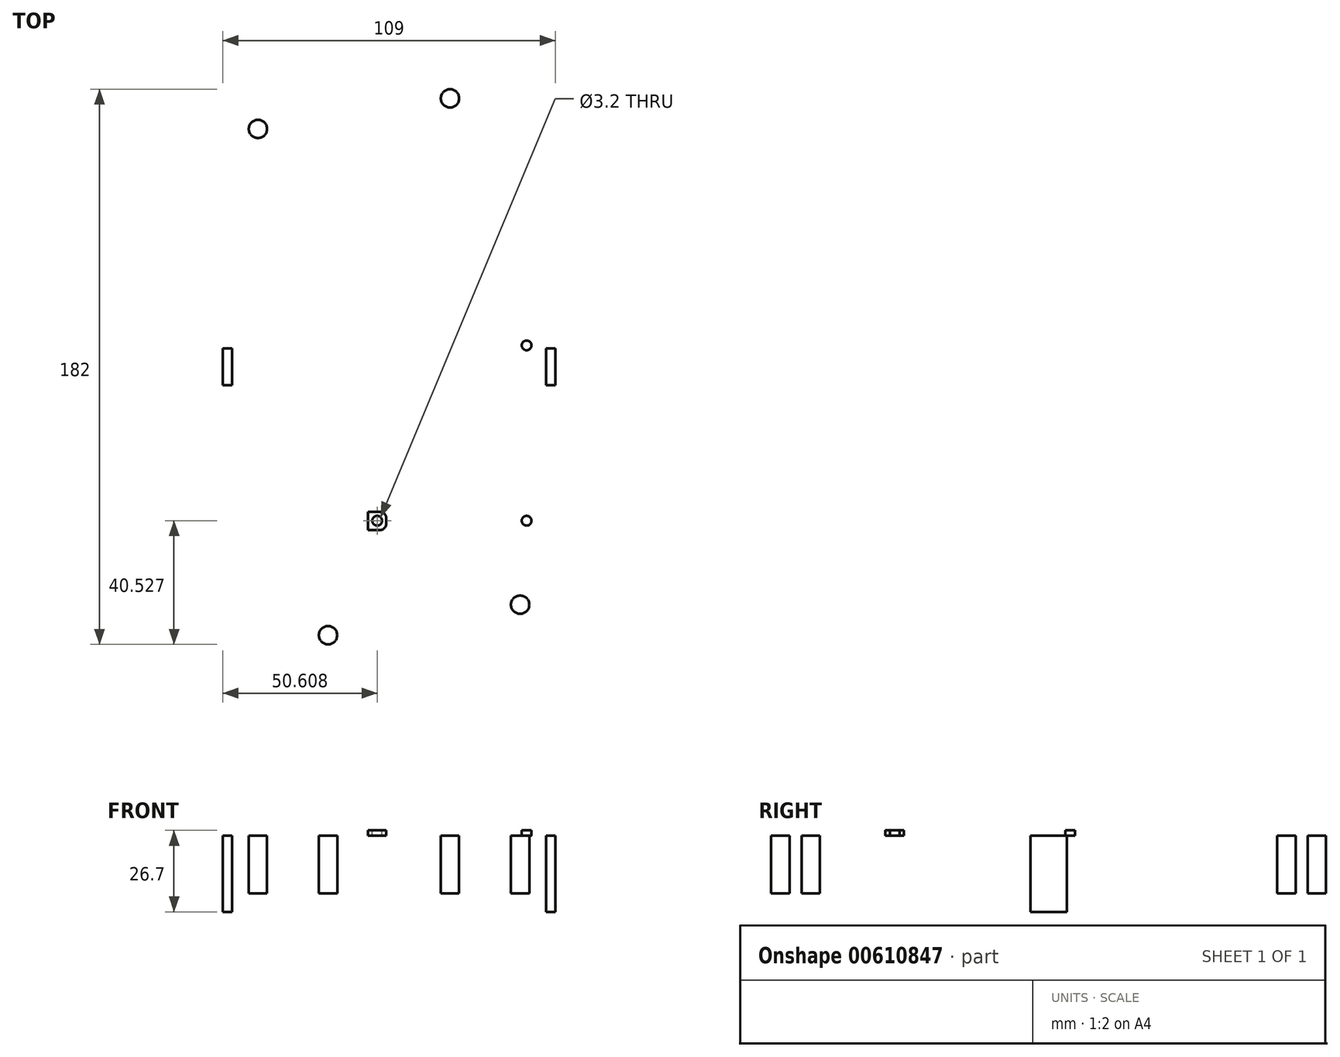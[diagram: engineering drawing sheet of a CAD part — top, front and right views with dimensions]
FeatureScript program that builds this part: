
annotation { "Feature Type Name" : "Feature", "Feature Type Description" : "" }
export const myFeature = defineFeature(function(context is Context, id is Id, definition is map)
    precondition{}
    {
        {
            var Q0;
            Q0=qCreatedBy(makeId("Top.planeOp"),FACE);
            var sketch = newSketch(context, id + "F0", { "sketchPlane" : qUnion([Q0])});
            skLineSegment(sketch, "E0.bottom", {"start": v(56, 96) * mm, "end": v(-56, 96) * mm});
            skLineSegment(sketch, "E0.top", {"start": v(56, -96) * mm, "end": v(-56, -96) * mm});
            skLineSegment(sketch, "E0.left", {"start": v(56, 96) * mm, "end": v(56, -96) * mm});
            skLineSegment(sketch, "E0.right", {"start": v(-56, 96) * mm, "end": v(-56, -96) * mm});
            skPoint(sketch, "E0.middle", {"position": v(0, 0) * mm});
            skLineSegment(sketch, "E1.MirrorCS", {"start": v(-41, 85) * mm, "end": v(-56, 85) * mm});
            skCircle(sketch, "E2.MirrorC", {"center": v(-43, 78) * mm, "radius": 1.6 * mm});
            skLineSegment(sketch, "E3", {"start": v(0, 96) * mm, "end": v(0, -96) * mm, "construction": true});
            skLineSegment(sketch, "E4", {"start": v(-36, 90) * mm, "end": v(-36, 96) * mm});
            skPoint(sketch, "E5.visualSharp", {"position": v(-36, 85) * mm});
            skArc(sketch, "E5.filletArc", {"start": v(-41, 85) * mm, "mid": v(-37.46, 86.46) * mm, "end": v(-36, 90) * mm});
            skArc(sketch, "E6.MirrorCS", {"start": v(41, 85) * mm, "mid": v(37.46, 86.46) * mm, "end": v(36, 90) * mm});
            skLineSegment(sketch, "E7.MirrorCS", {"start": v(41, 85) * mm, "end": v(56, 85) * mm});
            skLineSegment(sketch, "E8.MirrorCS", {"start": v(36, 90) * mm, "end": v(36, 96) * mm});
            skPoint(sketch, "E9.MirrorP", {"position": v(36, 85) * mm});
            skCircle(sketch, "E10.MirrorC", {"center": v(43, 78) * mm, "radius": 1.6 * mm});
            skLineSegment(sketch, "E11", {"start": v(-56, 0) * mm, "end": v(56, 0) * mm, "construction": true});
            skArc(sketch, "E12.MirrorCS", {"start": v(-41, -85) * mm, "mid": v(-37.46, -86.46) * mm, "end": v(-36, -90) * mm});
            skLineSegment(sketch, "E13.MirrorCS", {"start": v(-36, -90) * mm, "end": v(-36, -96) * mm});
            skLineSegment(sketch, "E14.MirrorCS", {"start": v(36, -90) * mm, "end": v(36, -96) * mm});
            skArc(sketch, "E15.MirrorCS", {"start": v(41, -85) * mm, "mid": v(37.46, -86.46) * mm, "end": v(36, -90) * mm});
            skCircle(sketch, "E16.MirrorC", {"center": v(-43, -78) * mm, "radius": 1.6 * mm});
            skLineSegment(sketch, "E17.MirrorCS", {"start": v(-41, -85) * mm, "end": v(-56, -85) * mm});
            skCircle(sketch, "E18.MirrorC", {"center": v(43, -78) * mm, "radius": 1.6 * mm});
            skPoint(sketch, "E19.MirrorP", {"position": v(36, -85) * mm});
            skLineSegment(sketch, "E20.MirrorCS", {"start": v(41, -85) * mm, "end": v(56, -85) * mm});
            skPoint(sketch, "E21.MirrorP", {"position": v(-36, -85) * mm});
            skCircle(sketch, "E22", {"center": v(-46, 7.1) * mm, "radius": 3 * mm});
            skCircle(sketch, "E23.1.0.0", {"center": v(-34, 7.1) * mm, "radius": 3 * mm});
            skCircle(sketch, "E23.2.0.0", {"center": v(-22, 7.1) * mm, "radius": 3 * mm});
            skLineSegment(sketch, "E23.direction1", {"start": v(-46, 7.1) * mm, "end": v(-34, 7.1) * mm, "construction": true});
            skCircle(sketch, "E24", {"center": v(-49, 0) * mm, "radius": 2 * mm});
            skCircle(sketch, "E25.1.0.0", {"center": v(-43, 0) * mm, "radius": 2 * mm});
            skLineSegment(sketch, "E25.direction1", {"start": v(-49, 0) * mm, "end": v(-43, 0) * mm, "construction": true});
            skCircle(sketch, "E26.1.0.0", {"center": v(-37, 0) * mm, "radius": 2 * mm});
            skCircle(sketch, "E26.1.0.1", {"center": v(-31, 0) * mm, "radius": 2 * mm});
            skCircle(sketch, "E26.2.0.0", {"center": v(-25, 0) * mm, "radius": 2 * mm});
            skCircle(sketch, "E26.2.0.1", {"center": v(-19, 0) * mm, "radius": 2 * mm});
            skLineSegment(sketch, "E26.direction1", {"start": v(-49, 0) * mm, "end": v(-37, 0) * mm, "construction": true});
            skSolve(sketch);
        }
        {
            var Q0;
            Q0=makeQuery(id+"F0.imprint","IMPRINT",FACE,{"disambiguationData":[TD([[makeQuery(id+"F0.imprint","IMPRINT",EDGE,{"derivedFrom":sQuery(id+"F0.wireOp",EDGE,"E0.bottom")}),1.0]])]});
            var sketch = newSketch(context, id + "F1", { "sketchPlane" : qUnion([Q0])});
            skLineSegment(sketch, "E27.bottom", {"start": v(-40.64, 23.04) * mm, "end": v(-40.64, 44.87) * mm});
            skLineSegment(sketch, "E27.left", {"start": v(-40.64, 23.04) * mm, "end": v(-19.64, 23.04) * mm});
            skLineSegment(sketch, "E27.right", {"start": v(-40.64, 73.84) * mm, "end": v(-19.64, 73.84) * mm});
            skPoint(sketch, "E27.middle", {"position": v(0, 48.44) * mm});
            skCircle(sketch, "E28", {"center": v(-37.14, 48.37) * mm, "radius": 1.59 * mm});
            skLineSegment(sketch, "E29.top", {"start": v(-33.64, 49.87) * mm, "end": v(-33.64, 46.87) * mm});
            skLineSegment(sketch, "E29.left", {"start": v(-40.64, 51.87) * mm, "end": v(-35.64, 51.87) * mm});
            skLineSegment(sketch, "E29.right", {"start": v(-40.64, 44.87) * mm, "end": v(-35.64, 44.87) * mm});
            skLineSegment(sketch, "E30", {"start": v(0, 23.04) * mm, "end": v(0, 25.04) * mm, "construction": true});
            skLineSegment(sketch, "E31.trimOffspring", {"start": v(-40.64, 51.87) * mm, "end": v(-40.64, 73.84) * mm});
            skLineSegment(sketch, "E32.MirrorCS", {"start": v(40.64, 23.04) * mm, "end": v(40.64, 44.87) * mm});
            skLineSegment(sketch, "E33.MirrorCS", {"start": v(40.64, 44.87) * mm, "end": v(35.64, 44.87) * mm});
            skLineSegment(sketch, "E34.MirrorCS", {"start": v(33.64, 49.87) * mm, "end": v(33.64, 46.87) * mm});
            skLineSegment(sketch, "E35.MirrorCS", {"start": v(40.64, 51.87) * mm, "end": v(35.64, 51.87) * mm});
            skLineSegment(sketch, "E36.MirrorCS", {"start": v(40.64, 51.87) * mm, "end": v(40.64, 73.84) * mm});
            skLineSegment(sketch, "E37.bottom", {"start": v(-19.64, 18.04) * mm, "end": v(-19.64, 18.04) * mm});
            skLineSegment(sketch, "E37.top", {"start": v(19.64, 18.04) * mm, "end": v(19.64, 18.04) * mm});
            skLineSegment(sketch, "E37.left", {"start": v(-17.64, 25.04) * mm, "end": v(17.64, 25.04) * mm});
            skLineSegment(sketch, "E38.trimOffspring", {"start": v(19.64, 23.04) * mm, "end": v(40.64, 23.04) * mm});
            skLineSegment(sketch, "E39.MirrorCS", {"start": v(-19.64, 68.84) * mm, "end": v(-19.64, 68.84) * mm});
            skLineSegment(sketch, "E40.MirrorCS", {"start": v(-17.64, 71.84) * mm, "end": v(17.64, 71.84) * mm});
            skLineSegment(sketch, "E41.MirrorCS", {"start": v(19.64, 68.84) * mm, "end": v(19.64, 68.84) * mm});
            skLineSegment(sketch, "E42.trimOffspring", {"start": v(19.64, 73.84) * mm, "end": v(40.64, 73.84) * mm});
            skPoint(sketch, "E43.visualSharp", {"position": v(-33.64, 51.87) * mm});
            skArc(sketch, "E43.filletArc", {"start": v(-33.64, 49.87) * mm, "mid": v(-34.22, 51.29) * mm, "end": v(-35.64, 51.87) * mm});
            skPoint(sketch, "E44.visualSharp", {"position": v(-33.64, 44.87) * mm});
            skArc(sketch, "E44.filletArc", {"start": v(-35.64, 44.87) * mm, "mid": v(-34.22, 45.46) * mm, "end": v(-33.64, 46.87) * mm});
            skPoint(sketch, "E45.visualSharp", {"position": v(33.64, 51.87) * mm});
            skArc(sketch, "E45.filletArc", {"start": v(35.64, 51.87) * mm, "mid": v(34.23, 51.29) * mm, "end": v(33.64, 49.87) * mm});
            skPoint(sketch, "E46.visualSharp", {"position": v(33.64, 44.87) * mm});
            skArc(sketch, "E46.filletArc", {"start": v(33.64, 46.87) * mm, "mid": v(34.23, 45.46) * mm, "end": v(35.64, 44.87) * mm});
            skPoint(sketch, "E47.visualSharp", {"position": v(-19.64, 25.04) * mm});
            skArc(sketch, "E47.filletArc", {"start": v(-17.64, 25.04) * mm, "mid": v(-19.05, 24.45) * mm, "end": v(-19.64, 23.04) * mm});
            skPoint(sketch, "E48.visualSharp", {"position": v(19.64, 25.04) * mm});
            skArc(sketch, "E48.filletArc", {"start": v(19.64, 23.04) * mm, "mid": v(19.06, 24.45) * mm, "end": v(17.64, 25.04) * mm});
            skPoint(sketch, "E49.visualSharp", {"position": v(-19.64, 71.84) * mm});
            skArc(sketch, "E49.filletArc", {"start": v(-19.64, 73.84) * mm, "mid": v(-19.05, 72.42) * mm, "end": v(-17.64, 71.84) * mm});
            skPoint(sketch, "E50.visualSharp", {"position": v(19.64, 71.84) * mm});
            skArc(sketch, "E50.filletArc", {"start": v(17.64, 71.84) * mm, "mid": v(19.06, 72.42) * mm, "end": v(19.64, 73.84) * mm});
            skCircle(sketch, "E51.MirrorC", {"center": v(37.14, 48.37) * mm, "radius": 1.59 * mm});
            skSolve(sketch);
        }
        {
            var Q0;
            Q0=makeQuery(id+"F0.imprint","IMPRINT",FACE,{"disambiguationData":[TD([[makeQuery(id+"F0.imprint","IMPRINT",EDGE,{"derivedFrom":sQuery(id+"F0.wireOp",EDGE,"mVZelFxc-g4tC-C0wc-Uz0j-Vh2jIqVkUQeU")}),-1.0]])]});
            var Q1;
            {var subQ2=sQuery(id+"F0.wireOp",EDGE,"E1.MirrorCS");Q1=makeQuery(id+"F0.imprint","IMPRINT",FACE,{"disambiguationData":[TD([[makeQuery(id+"F0.imprint","IMPRINT",EDGE,{"derivedFrom":subQ2}),1.0]])]});}
            extrude(context, id + "F2", {"entities" : qUnion([Q0, Q1]), "oppositeDirection" : true, "depth" : 1.7 * mm, "offsetDistance" : 25.4 * mm});
        }
        {
            var Q0;
            {var subQ2=sQuery(id+"F0.wireOp",EDGE,"E1.MirrorCS");Q0=makeQuery(id+"F0.imprint","IMPRINT",FACE,{"disambiguationData":[TD([[makeQuery(id+"F0.imprint","IMPRINT",EDGE,{"derivedFrom":subQ2}),1.0]])]});}
            var sketch = newSketch(context, id + "F3", { "sketchPlane" : qUnion([Q0])});
            skLineSegment(sketch, "E52.bottom", {"start": v(48.1, -74.97) * mm, "end": v(-6.9, -74.97) * mm});
            skLineSegment(sketch, "E52.top", {"start": v(42.15, 10.03) * mm, "end": v(26.6, 10.03) * mm});
            skLineSegment(sketch, "E52.left", {"start": v(48.1, -74.97) * mm, "end": v(48.1, 4.1) * mm});
            skLineSegment(sketch, "E52.right", {"start": v(-6.9, -74.97) * mm, "end": v(-6.9, 4.1) * mm});
            skPoint(sketch, "E52.middle", {"position": v(20.6, -32.47) * mm});
            skCircle(sketch, "E53", {"center": v(-3.9, 7.03) * mm, "radius": 1.6 * mm});
            skCircle(sketch, "E54", {"center": v(-3.9, -50.47) * mm, "radius": 1.6 * mm});
            skCircle(sketch, "E55.MirrorC", {"center": v(45.1, -50.47) * mm, "radius": 1.6 * mm});
            skPoint(sketch, "E56.middle", {"position": v(-3.94, 7.1) * mm});
            skLineSegment(sketch, "E57", {"start": v(-0.94, 10.1) * mm, "end": v(-0.94, 6.1) * mm});
            skLineSegment(sketch, "E58", {"start": v(-6.94, 4.1) * mm, "end": v(-2.94, 4.1) * mm});
            skPoint(sketch, "E59.orphan", {"position": v(-6.9, 10.03) * mm});
            skLineSegment(sketch, "E60.MirrorCS", {"start": v(42.15, 10.1) * mm, "end": v(42.15, 6.1) * mm});
            skLineSegment(sketch, "E61.MirrorCS", {"start": v(48.15, 4.1) * mm, "end": v(44.15, 4.1) * mm});
            skLineSegment(sketch, "E62.MirrorCS", {"start": v(-0.94, -51.54) * mm, "end": v(-0.94, -49.54) * mm});
            skLineSegment(sketch, "E63.MirrorCS", {"start": v(-6.94, -47.54) * mm, "end": v(-2.94, -47.54) * mm});
            skLineSegment(sketch, "E64.MirrorCS", {"start": v(48.15, -47.54) * mm, "end": v(44.15, -47.54) * mm});
            skLineSegment(sketch, "E65.MirrorCS", {"start": v(42.15, -51.54) * mm, "end": v(42.15, -49.54) * mm});
            skLineSegment(sketch, "E66", {"start": v(-2.94, -53.54) * mm, "end": v(-6.9, -53.54) * mm});
            skLineSegment(sketch, "E67", {"start": v(44.15, -53.54) * mm, "end": v(48.1, -53.54) * mm});
            skPoint(sketch, "E68.visualSharp", {"position": v(-0.94, 4.1) * mm});
            skArc(sketch, "E68.filletArc", {"start": v(-2.94, 4.1) * mm, "mid": v(-1.52, 4.68) * mm, "end": v(-0.94, 6.1) * mm});
            skPoint(sketch, "E69.visualSharp", {"position": v(42.15, 4.1) * mm});
            skArc(sketch, "E69.filletArc", {"start": v(42.15, 6.1) * mm, "mid": v(42.74, 4.68) * mm, "end": v(44.15, 4.1) * mm});
            skPoint(sketch, "E70.visualSharp", {"position": v(42.15, -47.54) * mm});
            skArc(sketch, "E70.filletArc", {"start": v(44.15, -47.54) * mm, "mid": v(42.74, -48.12) * mm, "end": v(42.15, -49.54) * mm});
            skPoint(sketch, "E71.visualSharp", {"position": v(42.15, -53.54) * mm});
            skArc(sketch, "E71.filletArc", {"start": v(42.15, -51.54) * mm, "mid": v(42.74, -52.95) * mm, "end": v(44.15, -53.54) * mm});
            skPoint(sketch, "E72.visualSharp", {"position": v(-0.94, -53.54) * mm});
            skArc(sketch, "E72.filletArc", {"start": v(-2.94, -53.54) * mm, "mid": v(-1.52, -52.95) * mm, "end": v(-0.94, -51.54) * mm});
            skPoint(sketch, "E73.visualSharp", {"position": v(-0.94, -47.54) * mm});
            skArc(sketch, "E73.filletArc", {"start": v(-0.94, -49.54) * mm, "mid": v(-1.52, -48.12) * mm, "end": v(-2.94, -47.54) * mm});
            skPoint(sketch, "E74.orphan", {"position": v(48.1, 10.03) * mm});
            skCircle(sketch, "E75.MirrorC", {"center": v(45.1, 7.03) * mm, "radius": 1.6 * mm});
            skLineSegment(sketch, "E76.top", {"start": v(14.6, 13.03) * mm, "end": v(26.6, 13.03) * mm});
            skLineSegment(sketch, "E76.left", {"start": v(14.6, 10.03) * mm, "end": v(14.6, 13.03) * mm});
            skLineSegment(sketch, "E76.right", {"start": v(26.6, 10.03) * mm, "end": v(26.6, 13.03) * mm});
            skLineSegment(sketch, "E77.trimOffspring", {"start": v(14.6, 10.03) * mm, "end": v(-0.94, 10.03) * mm});
            skLineSegment(sketch, "E78", {"start": v(20.6, 13.03) * mm, "end": v(20.6, -32.47) * mm, "construction": true});
            skSolve(sketch);
        }
        {
            var Q0;
            {var subQ10=sQuery(id+"F3.wireOp",EDGE,"E52.bottom");Q0=makeQuery(id+"F3.imprint","IMPRINT",FACE,{"disambiguationData":[TD([[makeQuery(id+"F3.imprint","IMPRINT",EDGE,{"derivedFrom":subQ10}),-1.0]])]});}
            var Q1;
            Q1=makeQuery(id+"F3.imprint","IMPRINT",FACE,{"disambiguationData":[TD([[makeQuery(id+"F3.imprint","IMPRINT",EDGE,{"derivedFrom":sQuery(id+"F3.wireOp",EDGE,"E54")}),1.0]])]});
            var Q2;
            Q2=makeQuery(id+"F3.imprint","IMPRINT",FACE,{"disambiguationData":[TD([[makeQuery(id+"F3.imprint","IMPRINT",EDGE,{"derivedFrom":sQuery(id+"F3.wireOp",EDGE,"E55.MirrorC")}),-1.0]])]});
            var Q3;
            Q3=makeQuery(id+"F3.imprint","IMPRINT",FACE,{"disambiguationData":[TD([[makeQuery(id+"F3.imprint","IMPRINT",EDGE,{"derivedFrom":sQuery(id+"F3.wireOp",EDGE,"E53")}),1.0]])]});
            var Q4;
            Q4=makeQuery(id+"F3.imprint","IMPRINT",FACE,{"disambiguationData":[TD([[makeQuery(id+"F3.imprint","IMPRINT",EDGE,{"derivedFrom":sQuery(id+"F3.wireOp",EDGE,"E75.MirrorC")}),-1.0]])]});
            extrude(context, id + "F4", {"entities" : qUnion([Q0, Q1, Q2, Q3, Q4]), "operationType" : NewBodyOperationType.REMOVE, "endBound" : BoundingType.THROUGH_ALL, "oppositeDirection" : true, "depth" : 25 * mm, "offsetDistance" : 25 * mm});
        }
        {
            var Q0;
            Q0=makeQuery(id+"F2.opExtrude","CAP_FACE",FACE,{"disambiguationData":[OSD([sQuery(id+"F0.wireOp",EDGE,"E0.bottom"),sQuery(id+"F0.wireOp",EDGE,"E0.top"),sQuery(id+"F0.wireOp",EDGE,"E0.left"),sQuery(id+"F0.wireOp",EDGE,"E0.right"),sQuery(id+"F0.wireOp",EDGE,"mVZelFxc-g4tC-C0wc-Uz0j-Vh2jIqVkUQeU"),sQuery(id+"F0.wireOp",EDGE,"M8He5rWl-kh4x-kdHM-IdgU-x27XWkE9IIy8"),sQuery(id+"F0.wireOp",EDGE,"rG5vQ4I5-FXk9-puCg-epYi-0rQccAZI7wWX"),sQuery(id+"F0.wireOp",EDGE,"e1ce7705-d192-41d6-9d17-3e3ea1f58656.filletArc"),sQuery(id+"F0.wireOp",EDGE,"a0c9e0a0-d2b6-48c2-8e4a-1fbf5c1a51ff0.MirrorCS"),sQuery(id+"F0.wireOp",EDGE,"79c2be4e-1c4e-47ff-9339-5f1860507eae0.MirrorCS"),sQuery(id+"F0.wireOp",EDGE,"E1.MirrorCS"),sQuery(id+"F0.wireOp",EDGE,"E2.MirrorC"),sQuery(id+"F0.wireOp",EDGE,"89904476-4486-4993-b36f-42ff1b67ea090.MirrorCS"),sQuery(id+"F0.wireOp",EDGE,"666ee2c6-ba1b-4df3-9c01-5a504d36f0380.MirrorCS"),sQuery(id+"F0.wireOp",EDGE,"cd7aaff7-76c4-4c00-b395-c9dec6d603b90.MirrorCS"),sQuery(id+"F0.wireOp",EDGE,"d5571941-fd82-42e1-a49e-1f228ba26ca00.MirrorC"),sQuery(id+"F0.wireOp",EDGE,"aba045b1-7084-4a47-9e29-d1e4a52ca4b50.MirrorCS"),sQuery(id+"F0.wireOp",EDGE,"385c2433-f9c0-4b01-a08a-10c937cdc7960.MirrorCS"),sQuery(id+"F0.wireOp",EDGE,"b24cfe77-ff9a-43eb-ac04-14a65a9553860.MirrorCS"),sQuery(id+"F0.wireOp",EDGE,"18466e08-046a-4d8b-9af7-ecd1c10ce6ca0.MirrorC")])],"isStart":false});
            var sketch = newSketch(context, id + "F5", { "sketchPlane" : qUnion([Q0])});
            skLineSegment(sketch, "E79", {"start": v(56, 0) * mm, "end": v(-56, 0) * mm, "construction": true});
            skLineSegment(sketch, "E80.bottom", {"start": v(54.5, -6) * mm, "end": v(51.5, -6) * mm});
            skLineSegment(sketch, "E80.top", {"start": v(54.5, 6) * mm, "end": v(51.5, 6) * mm});
            skLineSegment(sketch, "E80.left", {"start": v(54.5, -6) * mm, "end": v(54.5, 6) * mm});
            skLineSegment(sketch, "E80.right", {"start": v(51.5, -6) * mm, "end": v(51.5, 6) * mm});
            skPoint(sketch, "E80.middle", {"position": v(53, 0) * mm});
            skLineSegment(sketch, "E81.MirrorCS", {"start": v(-51.5, -6) * mm, "end": v(-51.5, 6) * mm});
            skLineSegment(sketch, "E82.MirrorCS", {"start": v(-54.5, -6) * mm, "end": v(-54.5, 6) * mm});
            skLineSegment(sketch, "E83.MirrorCS", {"start": v(-54.5, -6) * mm, "end": v(-51.5, -6) * mm});
            skLineSegment(sketch, "E84.MirrorCS", {"start": v(-54.5, 6) * mm, "end": v(-51.5, 6) * mm});
            skCircle(sketch, "E85", {"center": v(20, -88) * mm, "radius": 3 * mm});
            skCircle(sketch, "E86.MirrorC", {"center": v(-20, -88) * mm, "radius": 3 * mm});
            skCircle(sketch, "E87.MirrorC", {"center": v(-20, 88) * mm, "radius": 3 * mm});
            skCircle(sketch, "E88.MirrorC", {"center": v(20, 88) * mm, "radius": 3 * mm});
            skCircle(sketch, "E89", {"center": v(-43, -78) * mm, "radius": 3 * mm});
            skCircle(sketch, "E90.MirrorC", {"center": v(43, -78) * mm, "radius": 3 * mm});
            skCircle(sketch, "E91.MirrorC", {"center": v(43, 78) * mm, "radius": 3 * mm});
            skCircle(sketch, "E92.MirrorC", {"center": v(-43, 78) * mm, "radius": 3 * mm});
            skSolve(sketch);
        }
        {
            var Q0;
            Q0=makeQuery(id+"F5.imprint","IMPRINT",FACE,{"disambiguationData":[TD([[makeQuery(id+"F5.imprint","IMPRINT",EDGE,{"derivedFrom":sQuery(id+"F5.wireOp",EDGE,"tTqWljip-tRVv-SqzE-FBhO-0dZfNHrj9VjE")}),1.0]])]});
            var Q1;
            Q1=makeQuery(id+"F5.imprint","IMPRINT",FACE,{"disambiguationData":[TD([[makeQuery(id+"F5.imprint","IMPRINT",EDGE,{"derivedFrom":sQuery(id+"F5.wireOp",EDGE,"E87.MirrorC")}),1.0]])]});
            var Q2;
            Q2=makeQuery(id+"F5.imprint","IMPRINT",FACE,{"disambiguationData":[TD([[makeQuery(id+"F5.imprint","IMPRINT",EDGE,{"derivedFrom":sQuery(id+"F5.wireOp",EDGE,"E88.MirrorC")}),-1.0]])]});
            var Q3;
            Q3=makeQuery(id+"F5.imprint","IMPRINT",FACE,{"disambiguationData":[TD([[makeQuery(id+"F5.imprint","IMPRINT",EDGE,{"derivedFrom":sQuery(id+"F5.wireOp",EDGE,"rSkMEguS-4O09-OFhg-e29I-WYrAOI442o67")}),1.0]])]});
            var Q4;
            Q4=makeQuery(id+"F5.imprint","IMPRINT",FACE,{"disambiguationData":[TD([[makeQuery(id+"F5.imprint","IMPRINT",EDGE,{"derivedFrom":sQuery(id+"F5.wireOp",EDGE,"E86.MirrorC")}),-1.0]])]});
            var Q5;
            Q5=makeQuery(id+"F5.imprint","IMPRINT",FACE,{"disambiguationData":[TD([[makeQuery(id+"F5.imprint","IMPRINT",EDGE,{"derivedFrom":sQuery(id+"F5.wireOp",EDGE,"E85")}),1.0]])]});
            var Q6;
            Q6=makeQuery(id+"F5.imprint","IMPRINT",FACE,{"disambiguationData":[TD([[makeQuery(id+"F5.imprint","IMPRINT",EDGE,{"derivedFrom":sQuery(id+"F5.wireOp",EDGE,"LXKls5Zi-Srni-pf38-5cbD-jSPTRpKrrnaY")}),1.0]])]});
            var Q7;
            Q7=makeQuery(id+"F5.imprint","IMPRINT",FACE,{"disambiguationData":[TD([[makeQuery(id+"F5.imprint","IMPRINT",EDGE,{"derivedFrom":sQuery(id+"F5.wireOp",EDGE,"7hvn30T4-1R6D-S6KI-NifZ-XfE7Qp4TZYPN")}),1.0]])]});
            var Q8;
            Q8=makeQuery(id+"F5.imprint","IMPRINT",FACE,{"disambiguationData":[TD([[makeQuery(id+"F5.imprint","IMPRINT",EDGE,{"derivedFrom":sQuery(id+"F5.wireOp",EDGE,"E92.MirrorC")}),-1.0]])]});
            var Q9;
            Q9=makeQuery(id+"F5.imprint","IMPRINT",FACE,{"disambiguationData":[TD([[makeQuery(id+"F5.imprint","IMPRINT",EDGE,{"derivedFrom":sQuery(id+"F5.wireOp",EDGE,"E91.MirrorC")}),1.0]])]});
            var Q10;
            Q10=makeQuery(id+"F5.imprint","IMPRINT",FACE,{"disambiguationData":[TD([[makeQuery(id+"F5.imprint","IMPRINT",EDGE,{"derivedFrom":sQuery(id+"F5.wireOp",EDGE,"E90.MirrorC")}),-1.0]])]});
            var Q11;
            Q11=makeQuery(id+"F5.imprint","IMPRINT",FACE,{"disambiguationData":[TD([[makeQuery(id+"F5.imprint","IMPRINT",EDGE,{"derivedFrom":sQuery(id+"F5.wireOp",EDGE,"E89")}),1.0]])]});
            extrude(context, id + "F6", {"entities" : qUnion([Q0, Q1, Q2, Q3, Q4, Q5, Q6, Q7, Q8, Q9, Q10, Q11]), "operationType" : NewBodyOperationType.ADD, "depth" : 19 * mm, "offsetDistance" : 25 * mm});
        }
        {
            var Q0;
            Q0 = qSketchRegion(id + "F1", true);
            extrude(context, id + "F7", {"entities" : qUnion([Q0]), "operationType" : NewBodyOperationType.REMOVE, "endBound" : BoundingType.THROUGH_ALL, "oppositeDirection" : true, "depth" : 25 * mm, "offsetDistance" : 25 * mm});
        }
        {
            var Q0;
            Q0=makeQuery(id+"F5.imprint","IMPRINT",FACE,{"disambiguationData":[TD([[makeQuery(id+"F5.imprint","IMPRINT",EDGE,{"derivedFrom":sQuery(id+"F5.wireOp",EDGE,"E80.bottom")}),-1.0]])]});
            var Q1;
            Q1=makeQuery(id+"F5.imprint","IMPRINT",FACE,{"disambiguationData":[TD([[makeQuery(id+"F5.imprint","IMPRINT",EDGE,{"derivedFrom":sQuery(id+"F5.wireOp",EDGE,"E81.MirrorCS")}),1.0]])]});
            extrude(context, id + "F8", {"entities" : qUnion([Q0, Q1]), "operationType" : NewBodyOperationType.ADD, "depth" : 25 * mm, "offsetDistance" : 25 * mm});
        }
    });
